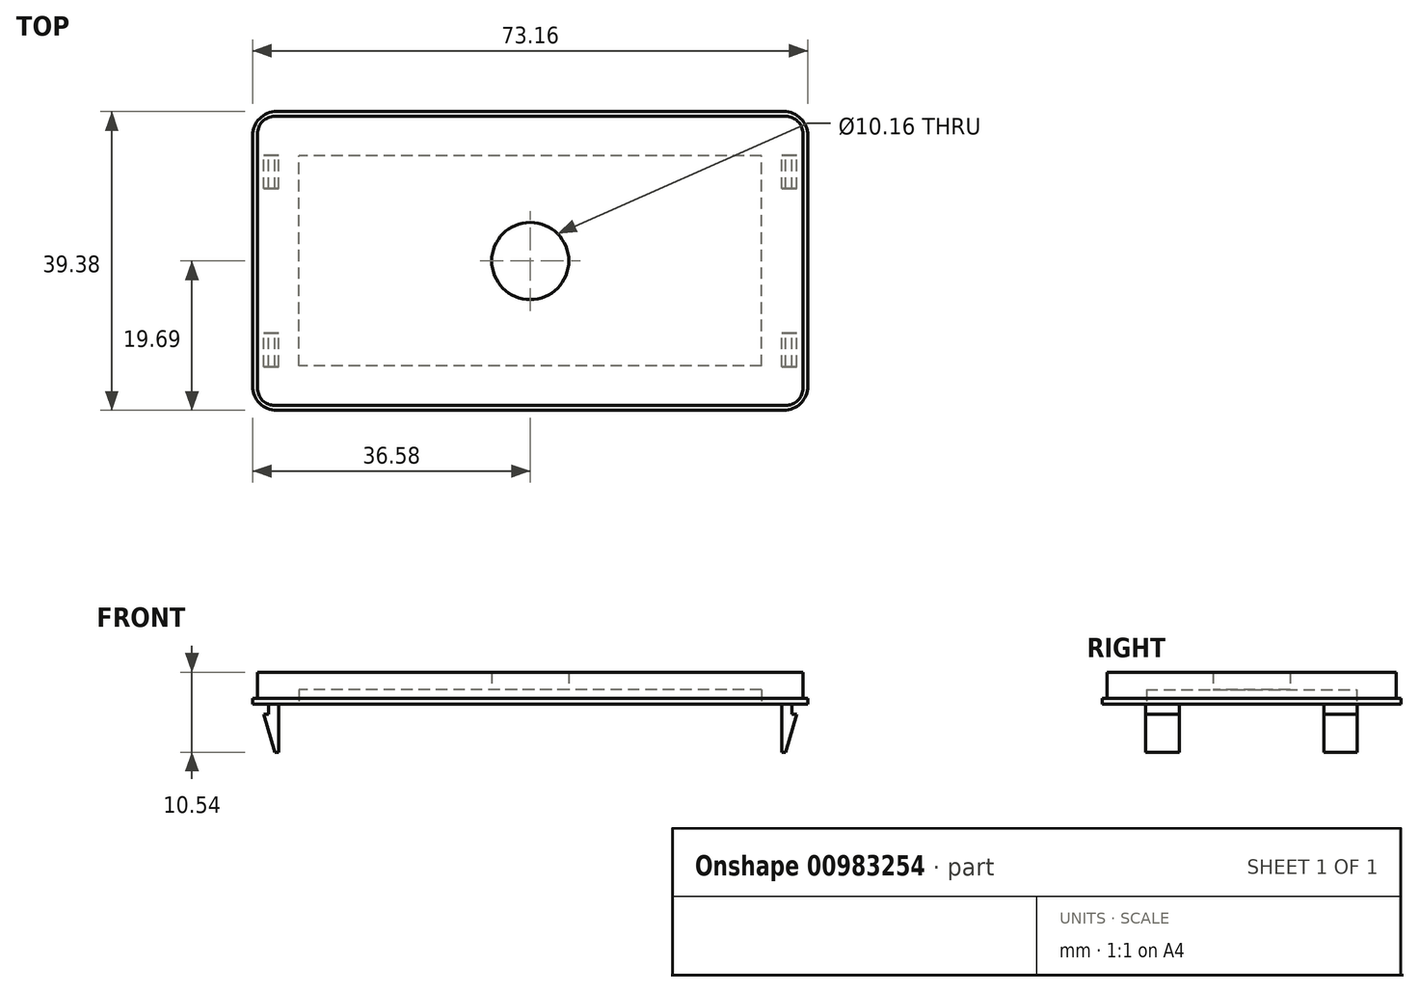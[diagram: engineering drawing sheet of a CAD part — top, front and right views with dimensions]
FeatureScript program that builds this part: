
annotation { "Feature Type Name" : "Feature", "Feature Type Description" : "" }
export const myFeature = defineFeature(function(context is Context, id is Id, definition is map)
    precondition{}
    {
        {
            var Q0;
            Q0=qCreatedBy(makeId("Top.planeOp"),FACE);
            var sketch = newSketch(context, id + "F0", { "sketchPlane" : qUnion([Q0])});
            skLineSegment(sketch, "E0.bottom", {"start": v(-33.4, 19.69) * mm, "end": v(33.4, 19.69) * mm});
            skLineSegment(sketch, "E0.top", {"start": v(-33.4, -19.69) * mm, "end": v(33.4, -19.69) * mm});
            skLineSegment(sketch, "E0.left", {"start": v(-36.58, 16.51) * mm, "end": v(-36.58, -16.51) * mm});
            skLineSegment(sketch, "E0.right", {"start": v(36.58, 16.51) * mm, "end": v(36.58, -16.51) * mm});
            skPoint(sketch, "E0.middle", {"position": v(0, 0) * mm});
            skCircle(sketch, "E1", {"center": v(0, 0) * mm, "radius": 5.08 * mm});
            skPoint(sketch, "E2.visualSharp", {"position": v(-36.58, 19.69) * mm});
            skArc(sketch, "E2.filletArc", {"start": v(-33.4, 19.69) * mm, "mid": v(-35.65, 18.76) * mm, "end": v(-36.58, 16.51) * mm});
            skPoint(sketch, "E3.visualSharp", {"position": v(-36.58, -19.69) * mm});
            skArc(sketch, "E3.filletArc", {"start": v(-36.58, -16.51) * mm, "mid": v(-35.65, -18.76) * mm, "end": v(-33.4, -19.69) * mm});
            skPoint(sketch, "E4.visualSharp", {"position": v(36.58, -19.69) * mm});
            skArc(sketch, "E4.filletArc", {"start": v(33.4, -19.68) * mm, "mid": v(35.65, -18.76) * mm, "end": v(36.58, -16.51) * mm});
            skPoint(sketch, "E5.visualSharp", {"position": v(36.58, 19.69) * mm});
            skArc(sketch, "E5.filletArc", {"start": v(36.58, 16.51) * mm, "mid": v(35.65, 18.76) * mm, "end": v(33.4, 19.68) * mm});
            skSolve(sketch);
        }
        {
            var Q0;
            Q0=makeQuery(id+"F0.imprint","IMPRINT",FACE,{"disambiguationData":[TD([[makeQuery(id+"F0.imprint","IMPRINT",EDGE,{"derivedFrom":sQuery(id+"F0.wireOp",EDGE,"E0.bottom")}),-1.0]])]});
            extrude(context, id + "F1", {"entities" : qUnion([Q0]), "depth" : 0.76 * mm, "offsetDistance" : 25.4 * mm});
        }
        {
            var Q0;
            Q0=qCreatedBy(makeId("Top.planeOp"),FACE);
            var sketch = newSketch(context, id + "F2", { "sketchPlane" : qUnion([Q0])});
            skLineSegment(sketch, "E6.bottom", {"start": v(-33.65, 19.05) * mm, "end": v(33.66, 19.05) * mm});
            skLineSegment(sketch, "E6.top", {"start": v(-33.66, -19.05) * mm, "end": v(33.66, -19.05) * mm});
            skLineSegment(sketch, "E6.left", {"start": v(-35.94, 16.76) * mm, "end": v(-35.94, -16.76) * mm});
            skLineSegment(sketch, "E6.right", {"start": v(35.94, 16.76) * mm, "end": v(35.94, -16.76) * mm});
            skPoint(sketch, "E6.middle", {"position": v(0, 0) * mm});
            skPoint(sketch, "E7.visualSharp", {"position": v(-35.94, 19.05) * mm});
            skArc(sketch, "E7.filletArc", {"start": v(-33.65, 19.05) * mm, "mid": v(-35.27, 18.38) * mm, "end": v(-35.94, 16.76) * mm});
            skPoint(sketch, "E8.visualSharp", {"position": v(-35.94, -19.05) * mm});
            skArc(sketch, "E8.filletArc", {"start": v(-35.94, -16.76) * mm, "mid": v(-35.27, -18.38) * mm, "end": v(-33.66, -19.05) * mm});
            skPoint(sketch, "E9.visualSharp", {"position": v(35.94, 19.05) * mm});
            skArc(sketch, "E9.filletArc", {"start": v(35.94, 16.76) * mm, "mid": v(35.27, 18.38) * mm, "end": v(33.66, 19.05) * mm});
            skPoint(sketch, "E10.visualSharp", {"position": v(35.94, -19.05) * mm});
            skArc(sketch, "E10.filletArc", {"start": v(33.66, -19.05) * mm, "mid": v(35.27, -18.38) * mm, "end": v(35.94, -16.76) * mm});
            skCircle(sketch, "E11", {"center": v(0, 0) * mm, "radius": 5.08 * mm});
            skSolve(sketch);
        }
        {
            var Q0;
            Q0 = qSketchRegion(id + "F2", true);
            extrude(context, id + "F3", {"entities" : qUnion([Q0]), "operationType" : NewBodyOperationType.ADD, "depth" : 4.2 * mm, "offsetDistance" : 25.4 * mm});
        }
        {
            var Q0;
            Q0=qCreatedBy(makeId("Top.planeOp"),FACE);
            var sketch = newSketch(context, id + "F4", { "sketchPlane" : qUnion([Q0])});
            skLineSegment(sketch, "E12.bottom", {"start": v(30.48, -13.84) * mm, "end": v(-30.48, -13.84) * mm});
            skLineSegment(sketch, "E12.top", {"start": v(30.48, 13.84) * mm, "end": v(-30.48, 13.84) * mm});
            skLineSegment(sketch, "E12.left", {"start": v(30.48, -13.84) * mm, "end": v(30.48, 13.84) * mm});
            skLineSegment(sketch, "E12.right", {"start": v(-30.48, -13.84) * mm, "end": v(-30.48, 13.84) * mm});
            skPoint(sketch, "E12.middle", {"position": v(0, 0) * mm});
            skSolve(sketch);
        }
        {
            var Q0;
            Q0=makeQuery(id+"F4.imprint","IMPRINT",FACE,{"disambiguationData":[TD([[makeQuery(id+"F4.imprint","IMPRINT",EDGE,{"derivedFrom":sQuery(id+"F4.wireOp",EDGE,"E12.bottom")}),-1.0]])]});
            extrude(context, id + "F5", {"entities" : qUnion([Q0]), "operationType" : NewBodyOperationType.REMOVE, "oppositeDirection" : true, "depth" : -1.88 * mm, "offsetDistance" : 25.4 * mm});
        }
        {
            var Q0;
            Q0=qCreatedBy(makeId("Front.planeOp"),FACE);
            var sketch = newSketch(context, id + "F6", { "sketchPlane" : qUnion([Q0])});
            skLineSegment(sketch, "E13", {"start": v(-34.48, 0) * mm, "end": v(-34.48, -1.35) * mm});
            skLineSegment(sketch, "E14", {"start": v(-34.48, -1.35) * mm, "end": v(-35.12, -1.35) * mm});
            skLineSegment(sketch, "E15", {"start": v(-35.12, -1.35) * mm, "end": v(-33.64, -6.35) * mm});
            skLineSegment(sketch, "E16", {"start": v(-33.64, -6.35) * mm, "end": v(-33.13, -6.35) * mm});
            skLineSegment(sketch, "E17", {"start": v(-33.13, -6.35) * mm, "end": v(-33.13, 0) * mm});
            skLineSegment(sketch, "E18", {"start": v(-33.13, 0) * mm, "end": v(-34.48, 0) * mm});
            skLineSegment(sketch, "E19.MirrorCS", {"start": v(33.13, -6.35) * mm, "end": v(33.13, 0) * mm});
            skLineSegment(sketch, "E20.MirrorCS", {"start": v(33.64, -6.35) * mm, "end": v(33.13, -6.35) * mm});
            skLineSegment(sketch, "E21.MirrorCS", {"start": v(35.12, -1.35) * mm, "end": v(33.64, -6.35) * mm});
            skLineSegment(sketch, "E22.MirrorCS", {"start": v(34.48, -1.35) * mm, "end": v(35.12, -1.35) * mm});
            skLineSegment(sketch, "E23.MirrorCS", {"start": v(34.48, 0) * mm, "end": v(34.48, -1.35) * mm});
            skLineSegment(sketch, "E24.MirrorCS", {"start": v(33.13, 0) * mm, "end": v(34.48, 0) * mm});
            skSolve(sketch);
        }
        {
            var Q0;
            Q0=makeQuery(id+"F6.imprint","IMPRINT",FACE,{"disambiguationData":[TD([[makeQuery(id+"F6.imprint","IMPRINT",EDGE,{"derivedFrom":sQuery(id+"F6.wireOp",EDGE,"E13")}),1.0]])]});
            var Q1;
            Q1=makeQuery(id+"F6.imprint","IMPRINT",FACE,{"disambiguationData":[TD([[makeQuery(id+"F6.imprint","IMPRINT",EDGE,{"derivedFrom":sQuery(id+"F6.wireOp",EDGE,"E19.MirrorCS")}),-1.0]])]});
            extrude(context, id + "F7", {"entities" : qUnion([Q0, Q1]), "operationType" : NewBodyOperationType.ADD, "endBound" : BoundingType.SYMMETRIC, "depth" : 27.86 * mm, "offsetDistance" : 25.4 * mm});
        }
        {
            var Q0;
            Q0=makeQuery(id+"F6.imprint","IMPRINT",FACE,{"disambiguationData":[TD([[makeQuery(id+"F6.imprint","IMPRINT",EDGE,{"derivedFrom":sQuery(id+"F6.wireOp",EDGE,"E13")}),1.0]])]});
            var Q1;
            Q1=makeQuery(id+"F6.imprint","IMPRINT",FACE,{"disambiguationData":[TD([[makeQuery(id+"F6.imprint","IMPRINT",EDGE,{"derivedFrom":sQuery(id+"F6.wireOp",EDGE,"E19.MirrorCS")}),-1.0]])]});
            extrude(context, id + "F8", {"entities" : qUnion([Q0, Q1]), "operationType" : NewBodyOperationType.REMOVE, "endBound" : BoundingType.SYMMETRIC, "depth" : 19.05 * mm, "offsetDistance" : 25.4 * mm});
        }
    });
